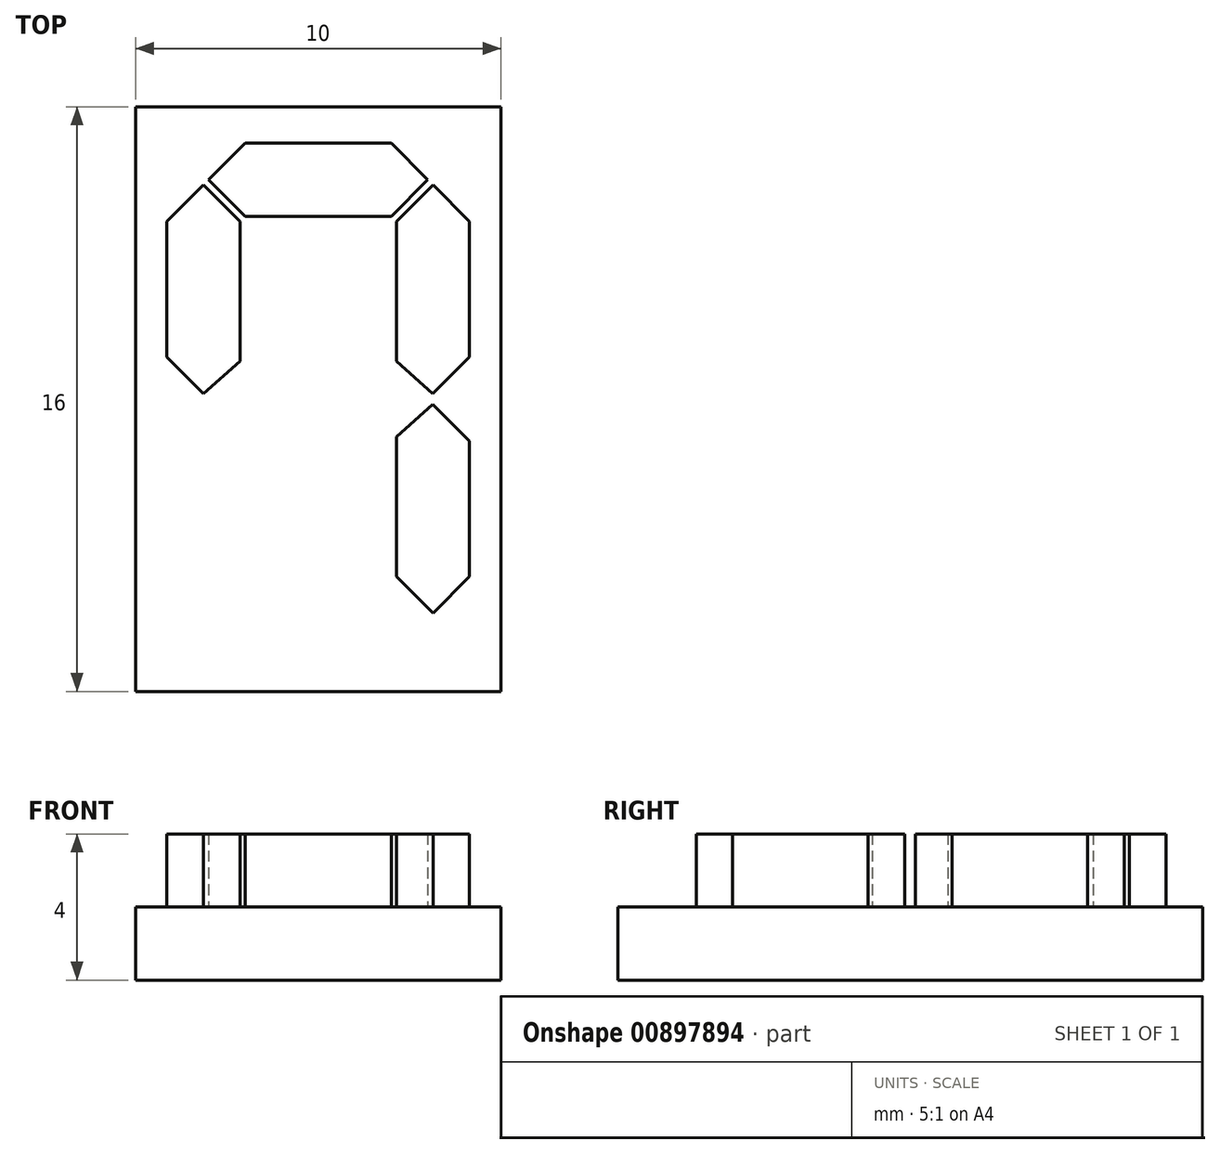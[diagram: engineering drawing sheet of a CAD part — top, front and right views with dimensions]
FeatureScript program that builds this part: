
annotation { "Feature Type Name" : "Feature", "Feature Type Description" : "" }
export const myFeature = defineFeature(function(context is Context, id is Id, definition is map)
    precondition{}
    {
        {
            var Q0;
            Q0=qCreatedBy(makeId("Top.planeOp"),FACE);
            var sketch = newSketch(context, id + "F0", { "sketchPlane" : qUnion([Q0])});
            skLineSegment(sketch, "E0.bottom", {"start": v(5, -8) * mm, "end": v(-5, -8) * mm});
            skLineSegment(sketch, "E0.top", {"start": v(5, 8) * mm, "end": v(-5, 8) * mm});
            skLineSegment(sketch, "E0.left", {"start": v(5, -8) * mm, "end": v(5, 8) * mm});
            skLineSegment(sketch, "E0.right", {"start": v(-5, -8) * mm, "end": v(-5, 8) * mm});
            skPoint(sketch, "E0.middle", {"position": v(0, 0) * mm});
            skSolve(sketch);
        }
        {
            var Q0;
            Q0=makeQuery(id+"F0.imprint","IMPRINT",FACE,{"disambiguationData":[TD([[makeQuery(id+"F0.imprint","IMPRINT",EDGE,{"derivedFrom":sQuery(id+"F0.wireOp",EDGE,"E0.bottom")}),-1.0]])]});
            extrude(context, id + "F1", {"entities" : qUnion([Q0]), "depth" : 2 * mm, "offsetDistance" : 25 * mm});
        }
        {
            var Q0;
            Q0=makeQuery(id+"F1.opExtrude","CAP_FACE",FACE,{"disambiguationData":[OSD([sQuery(id+"F0.wireOp",EDGE,"E0.bottom"),sQuery(id+"F0.wireOp",EDGE,"E0.top"),sQuery(id+"F0.wireOp",EDGE,"E0.left"),sQuery(id+"F0.wireOp",EDGE,"E0.right")])],"isStart":false});
            var sketch = newSketch(context, id + "F2", { "sketchPlane" : qUnion([Q0])});
            skLineSegment(sketch, "E1.direction2", {"start": v(-5, 7) * mm, "end": v(-5, 6) * mm, "construction": true});
            skLineSegment(sketch, "E2.direction1", {"start": v(-3, -8) * mm, "end": v(-2, -8) * mm, "construction": true});
            skLineSegment(sketch, "E3", {"start": v(-2, 7) * mm, "end": v(-3, 6) * mm});
            skLineSegment(sketch, "E4", {"start": v(-3, 6) * mm, "end": v(-2, 5) * mm});
            skLineSegment(sketch, "E5", {"start": v(-2, 5) * mm, "end": v(0, 5) * mm});
            skLineSegment(sketch, "E6", {"start": v(-2, 7) * mm, "end": v(0, 7) * mm});
            skLineSegment(sketch, "E7.0", {"start": v(-3.14, 5.86) * mm, "end": v(-2.14, 4.86) * mm});
            skLineSegment(sketch, "E8", {"start": v(-2.14, 4.86) * mm, "end": v(-2.14, 1.03) * mm});
            skLineSegment(sketch, "E9.0", {"start": v(-4.14, 4.86) * mm, "end": v(-4.14, 1.15) * mm});
            skLineSegment(sketch, "E10", {"start": v(-3.14, 5.86) * mm, "end": v(-4.14, 4.86) * mm});
            skLineSegment(sketch, "E11.0", {"start": v(-2.14, 1.03) * mm, "end": v(-3.14, 0.15) * mm});
            skLineSegment(sketch, "E12", {"start": v(-4.14, 1.15) * mm, "end": v(-3.14, 0.15) * mm});
            skLineSegment(sketch, "E13.MirrorCS", {"start": v(2, 7) * mm, "end": v(0, 7) * mm});
            skLineSegment(sketch, "E14.MirrorCS", {"start": v(2, 7) * mm, "end": v(3, 6) * mm});
            skLineSegment(sketch, "E15.MirrorCS", {"start": v(3, 6) * mm, "end": v(2, 5) * mm});
            skLineSegment(sketch, "E16.MirrorCS", {"start": v(2, 5) * mm, "end": v(0, 5) * mm});
            skLineSegment(sketch, "E17.MirrorCS", {"start": v(3.14, 5.86) * mm, "end": v(2.14, 4.86) * mm});
            skLineSegment(sketch, "E18.MirrorCS", {"start": v(3.14, 5.86) * mm, "end": v(4.14, 4.86) * mm});
            skLineSegment(sketch, "E19.MirrorCS", {"start": v(4.14, 4.86) * mm, "end": v(4.14, 1.15) * mm});
            skLineSegment(sketch, "E20.MirrorCS", {"start": v(4.14, 1.15) * mm, "end": v(3.14, 0.15) * mm});
            skLineSegment(sketch, "E21.MirrorCS", {"start": v(2.14, 4.86) * mm, "end": v(2.14, 1.03) * mm});
            skLineSegment(sketch, "E22.MirrorCS", {"start": v(2.14, 1.03) * mm, "end": v(3.14, 0.15) * mm});
            skLineSegment(sketch, "E23.MirrorCS", {"start": v(2.14, -1.03) * mm, "end": v(3.14, -0.15) * mm});
            skLineSegment(sketch, "E24.MirrorCS", {"start": v(4.14, -1.15) * mm, "end": v(3.14, -0.15) * mm});
            skLineSegment(sketch, "E25.MirrorCS", {"start": v(4.14, -4.86) * mm, "end": v(4.14, -1.15) * mm});
            skLineSegment(sketch, "E26.MirrorCS", {"start": v(2.14, -4.86) * mm, "end": v(2.14, -1.03) * mm});
            skLineSegment(sketch, "E27.MirrorCS", {"start": v(3.14, -5.86) * mm, "end": v(2.14, -4.86) * mm});
            skLineSegment(sketch, "E28.MirrorCS", {"start": v(3.14, -5.86) * mm, "end": v(4.14, -4.86) * mm});
            skSolve(sketch);
        }
        {
            var Q0;
            Q0=qSketchRegion(id+"F2",true);
            extrude(context, id + "F3", {"entities" : qUnion([Q0]), "operationType" : NewBodyOperationType.ADD, "depth" : 2 * mm, "offsetDistance" : 25 * mm});
        }
    });
